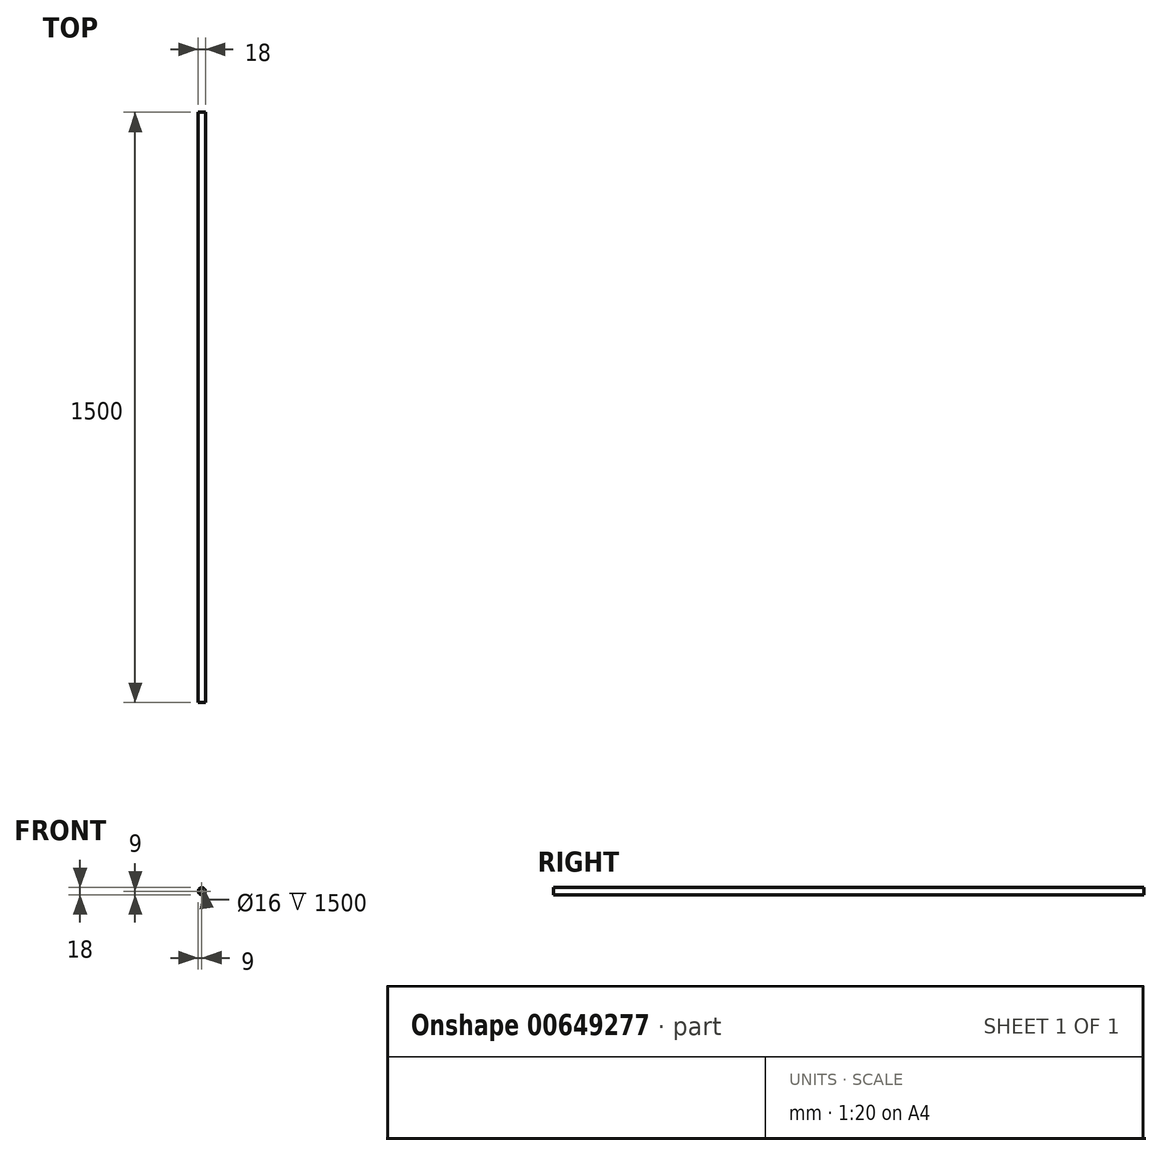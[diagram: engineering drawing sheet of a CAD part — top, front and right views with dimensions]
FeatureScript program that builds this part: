
annotation { "Feature Type Name" : "Feature", "Feature Type Description" : "" }
export const myFeature = defineFeature(function(context is Context, id is Id, definition is map)
    precondition{}
    {
        {
            var Q0;
            Q0=qCreatedBy(makeId("Front.planeOp"),FACE);
            var sketch = newSketch(context, id + "F0", { "sketchPlane" : qUnion([Q0])});
            skCircle(sketch, "E0", {"center": v(0, 0) * mm, "radius": 9 * mm});
            skCircle(sketch, "E1", {"center": v(0, 0) * mm, "radius": 8 * mm});
            skSolve(sketch);
        }
        {
            var Q0;
            Q0 = qSketchRegion(id + "F0", true);
            extrude(context, id + "F1", {"entities" : qUnion([Q0]), "depth" : 1500 * mm, "offsetDistance" : 25 * mm});
        }
    });
